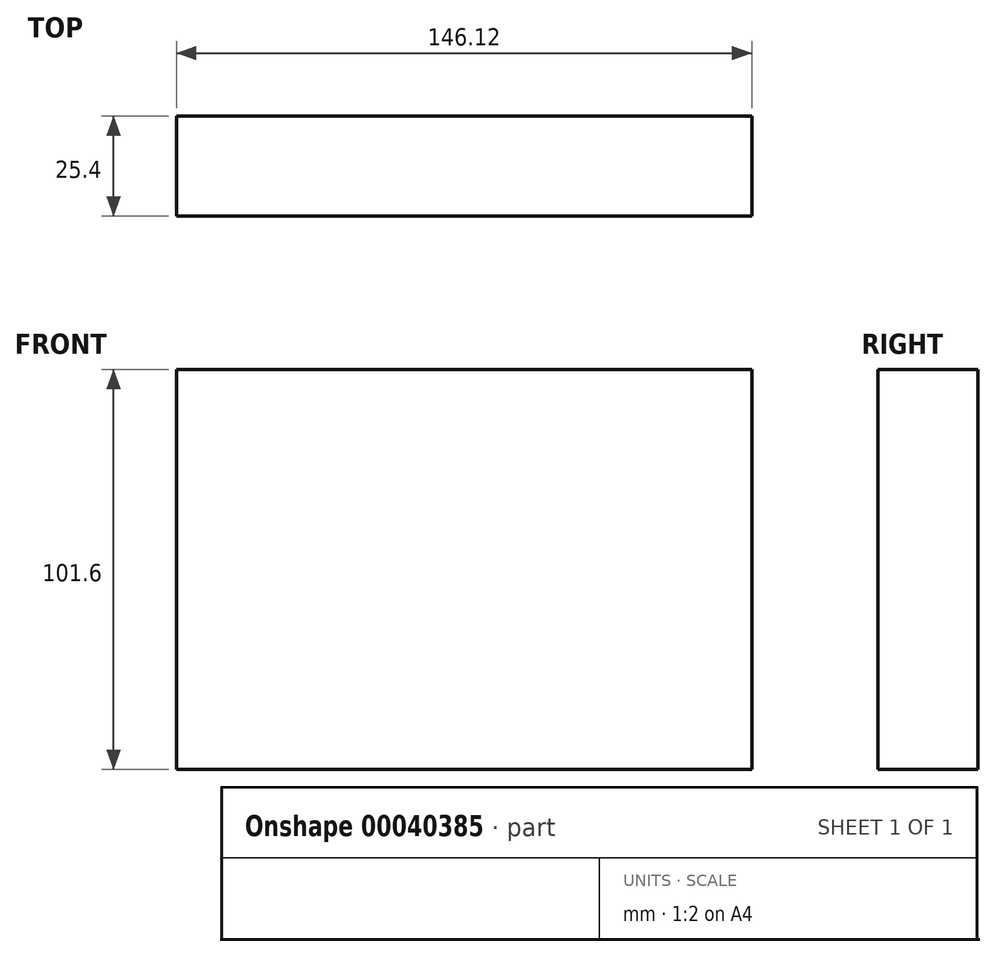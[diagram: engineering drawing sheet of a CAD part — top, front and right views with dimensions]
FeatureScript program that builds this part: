
annotation { "Feature Type Name" : "Feature", "Feature Type Description" : "" }
export const myFeature = defineFeature(function(context is Context, id is Id, definition is map)
    precondition{}
    {
        {
            var Q0;
            Q0=qCreatedBy(makeId("Front.planeOp"),FACE);
            var sketch = newSketch(context, id + "F0", { "sketchPlane" : qUnion([Q0])});
            skLineSegment(sketch, "E0.rect.bottom", {"start": v(73.06, 50.8) * mm, "end": v(-73.06, 50.8) * mm});
            skLineSegment(sketch, "E0.rect.top", {"start": v(73.06, -50.8) * mm, "end": v(-73.06, -50.8) * mm});
            skLineSegment(sketch, "E0.rect.left", {"start": v(73.06, 50.8) * mm, "end": v(73.06, -50.8) * mm});
            skLineSegment(sketch, "E0.rect.right", {"start": v(-73.06, 50.8) * mm, "end": v(-73.06, -50.8) * mm});
            skPoint(sketch, "E0.rect.middle", {"position": v(0, 0) * mm});
            skSolve(sketch);
        }
        {
            var Q0;
            Q0 = qSketchRegion(id + "F0", true);
            extrude(context, id + "F1", {"entities" : qUnion([Q0]), "depth" : 25.4 * mm});
        }
    });
